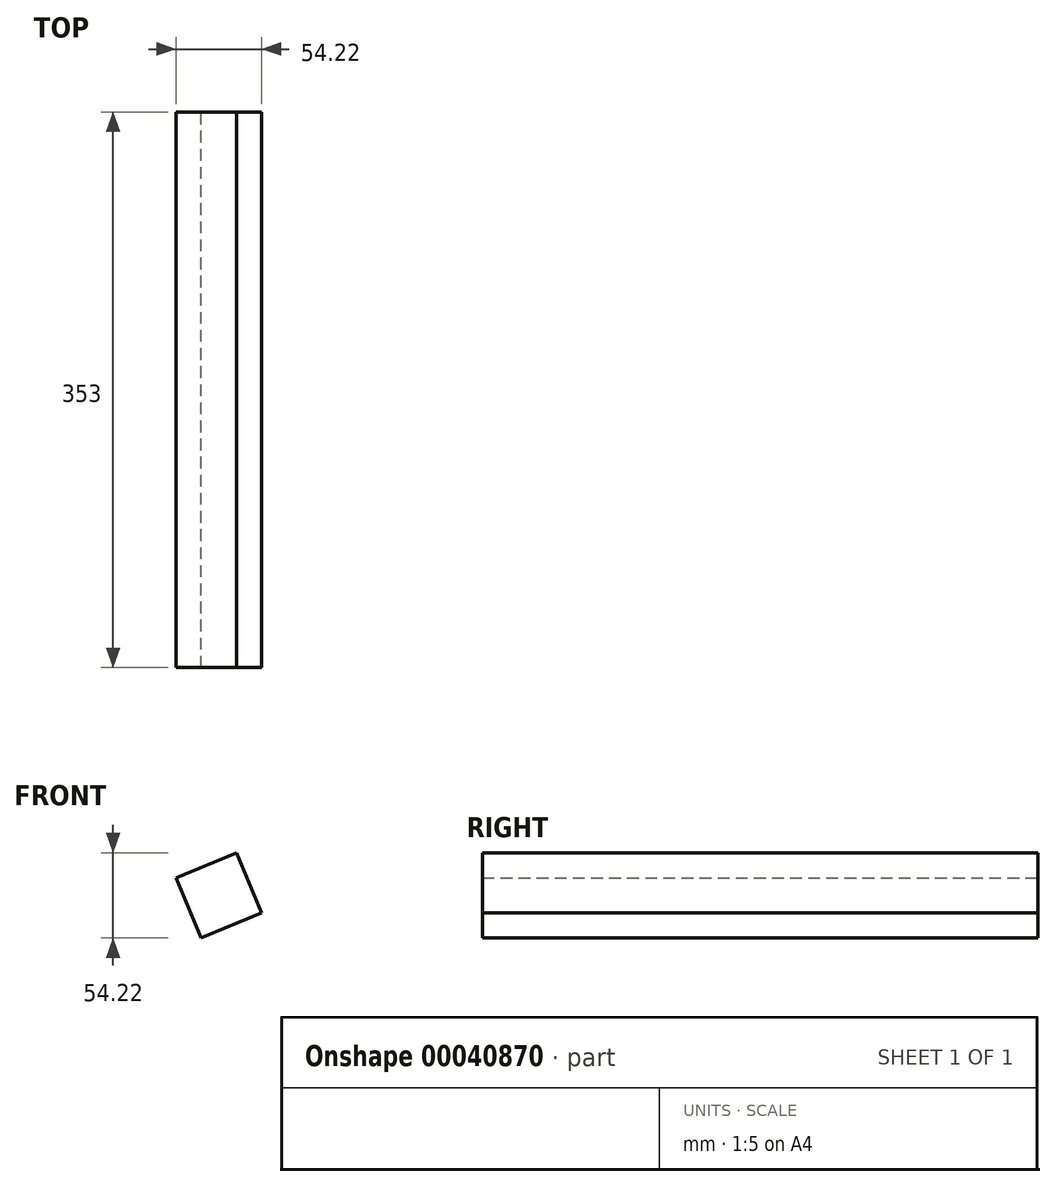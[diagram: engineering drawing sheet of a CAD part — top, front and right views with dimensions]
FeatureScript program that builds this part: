
annotation { "Feature Type Name" : "Feature", "Feature Type Description" : "" }
export const myFeature = defineFeature(function(context is Context, id is Id, definition is map)
    precondition{}
    {
        {
            var Q0;
            Q0=qCreatedBy(makeId("Front.planeOp"),FACE);
            var sketch = newSketch(context, id + "F0", { "sketchPlane" : qUnion([Q0])});
            skLineSegment(sketch, "E0.rect.bottom", {"start": v(11.23, 27.11) * mm, "end": v(-27.11, 11.23) * mm});
            skLineSegment(sketch, "E0.rect.left", {"start": v(11.23, 27.11) * mm, "end": v(27.11, -11.23) * mm});
            skLineSegment(sketch, "E0.rect.top", {"start": v(27.11, -11.23) * mm, "end": v(-11.23, -27.11) * mm});
            skLineSegment(sketch, "E0.rect.right", {"start": v(-27.11, 11.23) * mm, "end": v(-11.23, -27.11) * mm});
            skPoint(sketch, "E1", {"position": v(0, 0) * mm});
            skSolve(sketch);
        }
        {
            var Q0;
            Q0=makeQuery(id+"F0.imprint","IMPRINT",FACE,{"disambiguationData":[TD([[makeQuery(id+"F0.imprint","IMPRINT",EDGE,{"derivedFrom":sQuery(id+"F0.wireOp",EDGE,"E0.rect.bottom")}),1.0]])]});
            extrude(context, id + "F1", {"entities" : qUnion([Q0]), "depth" : 353 * mm});
        }
    });
